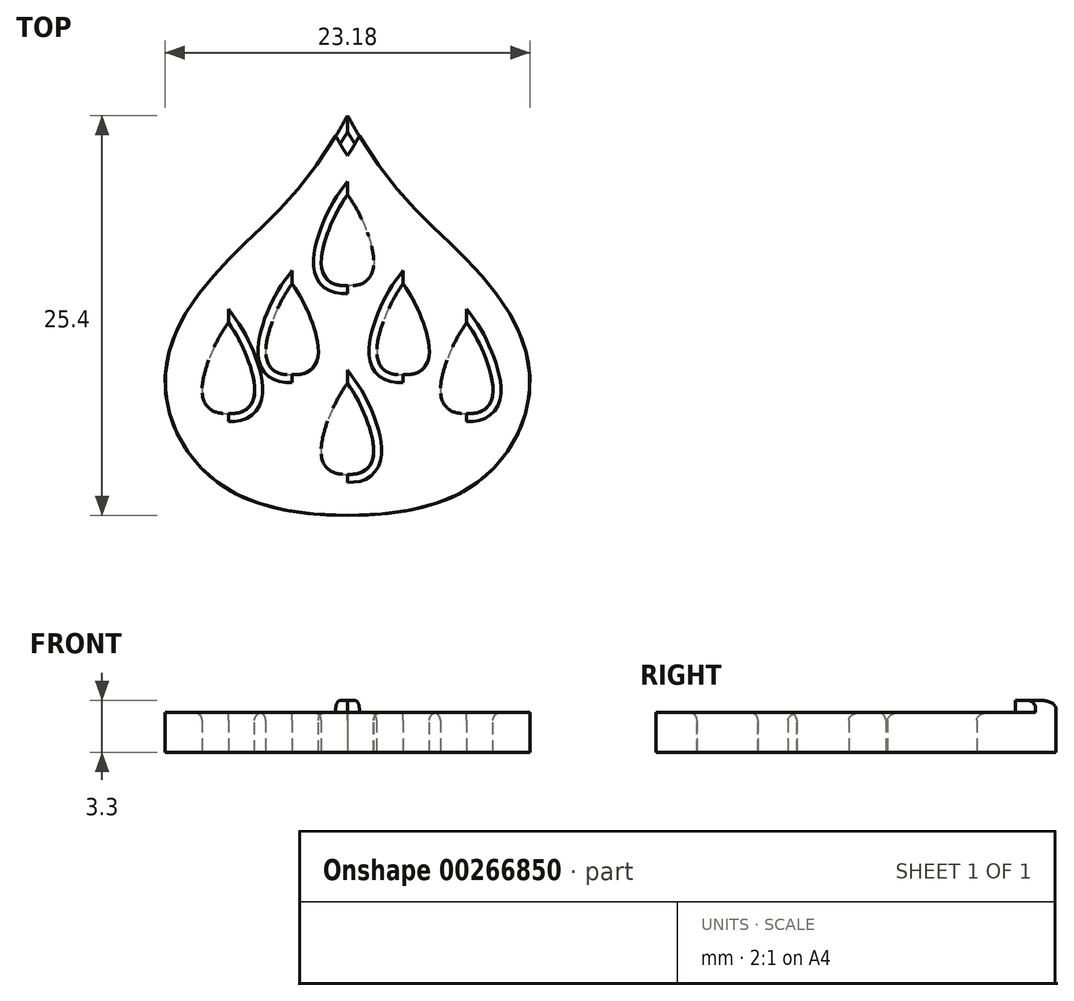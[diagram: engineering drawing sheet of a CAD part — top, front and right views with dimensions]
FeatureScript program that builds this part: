
annotation { "Feature Type Name" : "Feature", "Feature Type Description" : "" }
export const myFeature = defineFeature(function(context is Context, id is Id, definition is map)
    precondition{}
    {
        {
            var Q0;
            Q0=qCreatedBy(makeId("Top.planeOp"),FACE);
            var sketch = newSketch(context, id + "F0", { "sketchPlane" : qUnion([Q0])});
            skLineSegment(sketch, "E0.bottom", {"start": v(12.7, 12.7) * mm, "end": v(-12.7, 12.7) * mm, "construction": true});
            skLineSegment(sketch, "E0.top", {"start": v(12.7, -12.7) * mm, "end": v(-12.7, -12.7) * mm, "construction": true});
            skLineSegment(sketch, "E0.left", {"start": v(12.7, 12.7) * mm, "end": v(12.7, -12.7) * mm, "construction": true});
            skLineSegment(sketch, "E0.right", {"start": v(-12.7, 12.7) * mm, "end": v(-12.7, -12.7) * mm, "construction": true});
            skPoint(sketch, "E0.middle", {"position": v(0, 0) * mm});
            skLineSegment(sketch, "E1", {"start": v(0, 0) * mm, "end": v(0, 12.7) * mm});
            skFitSpline(sketch, "E2", {"points": [v(0, 12.7) * mm, v(-7.85, 3.25) * mm, v(-11.53, -3.23) * mm, v(-9.55, -9.42) * mm, v(0, -12.7) * mm], "startDerivative": vector(-29.48, -53.74) * mm, "endDerivative": vector(54.28, 0) * mm});
            skFitSpline(sketch, "E3.MirrorCS", {"points": [v(0, 12.7) * mm, v(7.85, 3.25) * mm, v(11.53, -3.23) * mm, v(9.55, -9.42) * mm, v(0, -12.7) * mm], "startDerivative": vector(29.48, -53.74) * mm, "endDerivative": vector(-54.28, 0) * mm});
            skSolve(sketch);
        }
        {
            var Q0;
            Q0 = qSketchRegion(id + "F0", true);
            extrude(context, id + "F1", {"entities" : qUnion([Q0]), "depth" : 2.54 * mm});
        }
        {
            var Q0;
            Q0=makeQuery(id+"F1.opExtrude","CAP_FACE",FACE,{"disambiguationData":[OSD([sQuery(id+"F0.wireOp",EDGE,"E2"),sQuery(id+"F0.wireOp",EDGE,"E3.MirrorCS")])],"isStart":false});
            var sketch = newSketch(context, id + "F2", { "sketchPlane" : qUnion([Q0])});
            skFitSpline(sketch, "E4.0", {"points": [v(1.11, 12.09) * mm, v(0.47, 10.91) * mm, v(-0.84, 8.96) * mm, v(-2.8, 6.92) * mm, v(-4.32, 5.7) * mm, v(-5.41, 4.86) * mm, v(-6.04, 4.34) * mm, v(-6.52, 3.92) * mm, v(-6.97, 3.47) * mm, v(-7.52, 2.86) * mm, v(-8.14, 2.04) * mm, v(-8.9, 0.85) * mm, v(-9.67, -0.74) * mm, v(-10.14, -2.37) * mm, v(-10.3, -3.58) * mm, v(-10.31, -4.75) * mm, v(-10.07, -6.12) * mm, v(-9.4, -7.6) * mm, v(-8.4, -8.88) * mm, v(-7.07, -9.94) * mm, v(-5.31, -10.76) * mm, v(-3.02, -11.3) * mm, v(-1.08, -11.43) * mm, v(0, -11.43) * mm]});
            skFitSpline(sketch, "E4.1", {"points": [v(-1.11, 12.09) * mm, v(-0.47, 10.91) * mm, v(0.84, 8.96) * mm, v(2.8, 6.92) * mm, v(4.32, 5.7) * mm, v(5.41, 4.86) * mm, v(6.04, 4.34) * mm, v(6.52, 3.92) * mm, v(6.97, 3.47) * mm, v(7.52, 2.86) * mm, v(8.14, 2.04) * mm, v(8.9, 0.85) * mm, v(9.67, -0.74) * mm, v(10.14, -2.37) * mm, v(10.3, -3.58) * mm, v(10.31, -4.75) * mm, v(10.07, -6.12) * mm, v(9.4, -7.6) * mm, v(8.4, -8.88) * mm, v(7.07, -9.94) * mm, v(5.31, -10.76) * mm, v(3.02, -11.3) * mm, v(1.08, -11.43) * mm, v(0, -11.43) * mm]});
            skFitSpline(sketch, "E5", {"points": [v(-3.29, 3.48) * mm, v(-4.95, 0.86) * mm, v(-5.27, -1.22) * mm, v(-3.29, -2.15) * mm], "startDerivative": vector(-5.74, -16) * mm, "endDerivative": vector(7.25, 0.42) * mm});
            skFitSpline(sketch, "E6.MirrorCS", {"points": [v(-3.29, 3.48) * mm, v(-1.63, 0.86) * mm, v(-1.31, -1.22) * mm, v(-3.29, -2.15) * mm], "startDerivative": vector(5.74, -16) * mm, "endDerivative": vector(-7.25, 0.42) * mm});
            skFitSpline(sketch, "E7", {"points": [v(-7.1, -1.24) * mm, v(-8.76, -3.85) * mm, v(-9.08, -5.94) * mm, v(-7.1, -6.87) * mm], "startDerivative": vector(-5.74, -16) * mm, "endDerivative": vector(7.25, 0.42) * mm});
            skFitSpline(sketch, "E8.MirrorCS", {"points": [v(-7.1, -1.24) * mm, v(-5.44, -3.85) * mm, v(-5.12, -5.94) * mm, v(-7.1, -6.87) * mm], "startDerivative": vector(5.74, -16) * mm, "endDerivative": vector(-7.25, 0.42) * mm});
            skFitSpline(sketch, "E9", {"points": [v(0.05, -4.16) * mm, v(-1.6, -6.77) * mm, v(-1.93, -8.85) * mm, v(0.05, -9.78) * mm], "startDerivative": vector(-5.74, -16) * mm, "endDerivative": vector(7.25, 0.42) * mm});
            skFitSpline(sketch, "E10.MirrorCS", {"points": [v(0.05, -4.16) * mm, v(1.7, -6.77) * mm, v(2.03, -8.85) * mm, v(0.05, -9.78) * mm], "startDerivative": vector(5.74, -16) * mm, "endDerivative": vector(-7.25, 0.42) * mm});
            skFitSpline(sketch, "E11", {"points": [v(0.05, 8.08) * mm, v(-1.6, 5.47) * mm, v(-1.93, 3.39) * mm, v(0.05, 2.46) * mm], "startDerivative": vector(-5.74, -16) * mm, "endDerivative": vector(7.25, 0.42) * mm});
            skFitSpline(sketch, "E12.MirrorCS", {"points": [v(0.05, 8.08) * mm, v(1.7, 5.47) * mm, v(2.03, 3.39) * mm, v(0.05, 2.46) * mm], "startDerivative": vector(5.74, -16) * mm, "endDerivative": vector(-7.25, 0.42) * mm});
            skLineSegment(sketch, "E13", {"start": v(0, 10.2) * mm, "end": v(0, 12.7) * mm});
            skFitSpline(sketch, "E14.MirrorCS", {"points": [v(7.1, -1.24) * mm, v(5.44, -3.85) * mm, v(5.12, -5.94) * mm, v(7.1, -6.87) * mm], "startDerivative": vector(-5.74, -16) * mm, "endDerivative": vector(7.25, 0.42) * mm});
            skFitSpline(sketch, "E15.MirrorCS", {"points": [v(7.1, -1.24) * mm, v(8.76, -3.85) * mm, v(9.08, -5.94) * mm, v(7.1, -6.87) * mm], "startDerivative": vector(5.74, -16) * mm, "endDerivative": vector(-7.25, 0.42) * mm});
            skFitSpline(sketch, "E16.MirrorCS", {"points": [v(3.29, 3.48) * mm, v(4.95, 0.86) * mm, v(5.27, -1.22) * mm, v(3.29, -2.15) * mm], "startDerivative": vector(5.74, -16) * mm, "endDerivative": vector(-7.25, 0.42) * mm});
            skFitSpline(sketch, "E17.MirrorCS", {"points": [v(3.29, 3.48) * mm, v(1.63, 0.86) * mm, v(1.31, -1.22) * mm, v(3.29, -2.15) * mm], "startDerivative": vector(-5.74, -16) * mm, "endDerivative": vector(7.25, 0.42) * mm});
            skSolve(sketch);
        }
        {
            var Q0;
            Q0=makeQuery(id+"F2.imprint","IMPRINT",FACE,{"disambiguationData":[TD([[makeQuery(id+"F2.imprint","IMPRINT",EDGE,{"derivedFrom":sQuery(id+"F2.wireOp",EDGE,"E4.0")}),-1.0]])]});
            extrude(context, id + "F3", {"entities" : qUnion([Q0]), "operationType" : NewBodyOperationType.ADD, "depth" : 0.76 * mm});
        }
        {
            var Q0;
            Q0=qCreatedBy(makeId("Top.planeOp"),FACE);
            var sketch = newSketch(context, id + "F4", { "sketchPlane" : qUnion([Q0])});
            skFitSpline(sketch, "E18", {"points": [v(0, 7.67) * mm, v(-1.66, 3.17) * mm, v(-0.92, 2.03) * mm, v(0, 1.9) * mm], "startDerivative": vector(-5.41, -7.3) * mm, "endDerivative": vector(3.85, 0.13) * mm});
            skLineSegment(sketch, "E19", {"start": v(0, 7.67) * mm, "end": v(0, 1.9) * mm});
            skFitSpline(sketch, "E20.MirrorCS", {"points": [v(0, 7.67) * mm, v(1.66, 3.17) * mm, v(0.92, 2.03) * mm, v(0, 1.9) * mm], "startDerivative": vector(5.41, -7.3) * mm, "endDerivative": vector(-3.85, 0.13) * mm});
            skFitSpline(sketch, "E21", {"points": [v(-0.01, -4.32) * mm, v(-1.67, -8.82) * mm, v(-0.93, -9.95) * mm, v(-0.01, -10.09) * mm], "startDerivative": vector(-5.41, -7.3) * mm, "endDerivative": vector(3.85, 0.13) * mm});
            skFitSpline(sketch, "E22.MirrorCS", {"points": [v(-0.01, -4.32) * mm, v(1.65, -8.82) * mm, v(0.9, -9.95) * mm, v(-0.01, -10.09) * mm], "startDerivative": vector(5.41, -7.3) * mm, "endDerivative": vector(-3.85, 0.13) * mm});
            skFitSpline(sketch, "E23", {"points": [v(-3.53, 2.01) * mm, v(-5.19, -2.5) * mm, v(-4.44, -3.63) * mm, v(-3.53, -3.76) * mm], "startDerivative": vector(-5.41, -7.3) * mm, "endDerivative": vector(3.85, 0.13) * mm});
            skFitSpline(sketch, "E24.MirrorCS", {"points": [v(-3.53, 2.01) * mm, v(-1.86, -2.5) * mm, v(-2.6, -3.63) * mm, v(-3.53, -3.76) * mm], "startDerivative": vector(5.41, -7.3) * mm, "endDerivative": vector(-3.85, 0.13) * mm});
            skFitSpline(sketch, "E25", {"points": [v(-7.57, -0.45) * mm, v(-9.23, -4.95) * mm, v(-8.49, -6.1) * mm, v(-7.57, -6.22) * mm], "startDerivative": vector(-5.41, -7.3) * mm, "endDerivative": vector(3.85, 0.13) * mm});
            skFitSpline(sketch, "E26.MirrorCS", {"points": [v(-7.57, -0.45) * mm, v(-5.9, -4.95) * mm, v(-6.65, -6.1) * mm, v(-7.57, -6.22) * mm], "startDerivative": vector(5.41, -7.3) * mm, "endDerivative": vector(-3.85, 0.13) * mm});
            skFitSpline(sketch, "E27.MirrorCS", {"points": [v(3.53, 2.01) * mm, v(1.86, -2.5) * mm, v(2.6, -3.63) * mm, v(3.53, -3.76) * mm], "startDerivative": vector(-5.41, -7.3) * mm, "endDerivative": vector(3.85, 0.13) * mm});
            skFitSpline(sketch, "E28.MirrorCS", {"points": [v(3.53, 2.01) * mm, v(5.19, -2.5) * mm, v(4.44, -3.63) * mm, v(3.53, -3.76) * mm], "startDerivative": vector(5.41, -7.3) * mm, "endDerivative": vector(-3.85, 0.13) * mm});
            skFitSpline(sketch, "E29.MirrorCS", {"points": [v(7.57, -0.45) * mm, v(5.9, -4.95) * mm, v(6.65, -6.1) * mm, v(7.57, -6.22) * mm], "startDerivative": vector(-5.41, -7.3) * mm, "endDerivative": vector(3.85, 0.13) * mm});
            skFitSpline(sketch, "E30.MirrorCS", {"points": [v(7.57, -0.45) * mm, v(9.23, -4.95) * mm, v(8.49, -6.1) * mm, v(7.57, -6.22) * mm], "startDerivative": vector(5.41, -7.3) * mm, "endDerivative": vector(-3.85, 0.13) * mm});
            skSolve(sketch);
        }
        {
            var Q0;
            Q0 = qSketchRegion(id + "F4", true);
            extrude(context, id + "F5", {"entities" : qUnion([Q0]), "operationType" : NewBodyOperationType.REMOVE, "depth" : 25.4 * mm});
        }
        {
            var Q0;
            Q0=makeQuery(id+"F3.opExtrude","CAP_EDGE",EDGE,{"disambiguationData":[OSD([sQuery(id+"F0.wireOp",EDGE,"E2")])],"isStart":false});
            var Q1;
            Q1=makeQuery(id+"F3.opExtrude","CAP_EDGE",EDGE,{"disambiguationData":[OSD([sQuery(id+"F0.wireOp",EDGE,"E3.MirrorCS")])],"isStart":false});
            var Q2;
            Q2=makeQuery(id+"F5.boolean.opBoolean","INTERSECT",EDGE,{"derivedFrom":[makeQuery(id+"F1.opExtrude","CAP_FACE",FACE,{"disambiguationData":[OSD([sQuery(id+"F0.wireOp",EDGE,"E2"),sQuery(id+"F0.wireOp",EDGE,"E3.MirrorCS")])],"isStart":false}),makeQuery(id+"F5.opExtrude","SWEPT_FACE",FACE,{"disambiguationData":[OSD([sQuery(id+"F4.wireOp",EDGE,"E23")])]})]});
            var Q3;
            Q3=makeQuery(id+"F5.boolean.opBoolean","INTERSECT",EDGE,{"derivedFrom":[makeQuery(id+"F1.opExtrude","CAP_FACE",FACE,{"disambiguationData":[OSD([sQuery(id+"F0.wireOp",EDGE,"E2"),sQuery(id+"F0.wireOp",EDGE,"E3.MirrorCS")])],"isStart":false}),makeQuery(id+"F5.opExtrude","SWEPT_FACE",FACE,{"disambiguationData":[OSD([sQuery(id+"F4.wireOp",EDGE,"E24.MirrorCS")])]})]});
            var Q4;
            Q4=makeQuery(id+"F5.boolean.opBoolean","INTERSECT",EDGE,{"derivedFrom":[makeQuery(id+"F1.opExtrude","CAP_FACE",FACE,{"disambiguationData":[OSD([sQuery(id+"F0.wireOp",EDGE,"E2"),sQuery(id+"F0.wireOp",EDGE,"E3.MirrorCS")])],"isStart":false}),makeQuery(id+"F5.opExtrude","SWEPT_FACE",FACE,{"disambiguationData":[OSD([sQuery(id+"F4.wireOp",EDGE,"E18")])]})]});
            var Q5;
            Q5=makeQuery(id+"F5.boolean.opBoolean","INTERSECT",EDGE,{"derivedFrom":[makeQuery(id+"F1.opExtrude","CAP_FACE",FACE,{"disambiguationData":[OSD([sQuery(id+"F0.wireOp",EDGE,"E2"),sQuery(id+"F0.wireOp",EDGE,"E3.MirrorCS")])],"isStart":false}),makeQuery(id+"F5.opExtrude","SWEPT_FACE",FACE,{"disambiguationData":[OSD([sQuery(id+"F4.wireOp",EDGE,"E20.MirrorCS")])]})]});
            var Q6;
            Q6=makeQuery(id+"F5.boolean.opBoolean","INTERSECT",EDGE,{"derivedFrom":[makeQuery(id+"F1.opExtrude","CAP_FACE",FACE,{"disambiguationData":[OSD([sQuery(id+"F0.wireOp",EDGE,"E2"),sQuery(id+"F0.wireOp",EDGE,"E3.MirrorCS")])],"isStart":false}),makeQuery(id+"F5.opExtrude","SWEPT_FACE",FACE,{"disambiguationData":[OSD([sQuery(id+"F4.wireOp",EDGE,"E27.MirrorCS")])]})]});
            var Q7;
            Q7=makeQuery(id+"F5.boolean.opBoolean","INTERSECT",EDGE,{"derivedFrom":[makeQuery(id+"F1.opExtrude","CAP_FACE",FACE,{"disambiguationData":[OSD([sQuery(id+"F0.wireOp",EDGE,"E2"),sQuery(id+"F0.wireOp",EDGE,"E3.MirrorCS")])],"isStart":false}),makeQuery(id+"F5.opExtrude","SWEPT_FACE",FACE,{"disambiguationData":[OSD([sQuery(id+"F4.wireOp",EDGE,"E28.MirrorCS")])]})]});
            var Q8;
            Q8=makeQuery(id+"F5.boolean.opBoolean","INTERSECT",EDGE,{"derivedFrom":[makeQuery(id+"F1.opExtrude","CAP_FACE",FACE,{"disambiguationData":[OSD([sQuery(id+"F0.wireOp",EDGE,"E2"),sQuery(id+"F0.wireOp",EDGE,"E3.MirrorCS")])],"isStart":false}),makeQuery(id+"F5.opExtrude","SWEPT_FACE",FACE,{"disambiguationData":[OSD([sQuery(id+"F4.wireOp",EDGE,"E30.MirrorCS")])]})]});
            var Q9;
            Q9=makeQuery(id+"F5.boolean.opBoolean","INTERSECT",EDGE,{"derivedFrom":[makeQuery(id+"F1.opExtrude","CAP_FACE",FACE,{"disambiguationData":[OSD([sQuery(id+"F0.wireOp",EDGE,"E2"),sQuery(id+"F0.wireOp",EDGE,"E3.MirrorCS")])],"isStart":false}),makeQuery(id+"F5.opExtrude","SWEPT_FACE",FACE,{"disambiguationData":[OSD([sQuery(id+"F4.wireOp",EDGE,"E29.MirrorCS")])]})]});
            var Q10;
            Q10=makeQuery(id+"F5.boolean.opBoolean","INTERSECT",EDGE,{"derivedFrom":[makeQuery(id+"F1.opExtrude","CAP_FACE",FACE,{"disambiguationData":[OSD([sQuery(id+"F0.wireOp",EDGE,"E2"),sQuery(id+"F0.wireOp",EDGE,"E3.MirrorCS")])],"isStart":false}),makeQuery(id+"F5.opExtrude","SWEPT_FACE",FACE,{"disambiguationData":[OSD([sQuery(id+"F4.wireOp",EDGE,"E22.MirrorCS")])]})]});
            var Q11;
            Q11=makeQuery(id+"F5.boolean.opBoolean","INTERSECT",EDGE,{"derivedFrom":[makeQuery(id+"F1.opExtrude","CAP_FACE",FACE,{"disambiguationData":[OSD([sQuery(id+"F0.wireOp",EDGE,"E2"),sQuery(id+"F0.wireOp",EDGE,"E3.MirrorCS")])],"isStart":false}),makeQuery(id+"F5.opExtrude","SWEPT_FACE",FACE,{"disambiguationData":[OSD([sQuery(id+"F4.wireOp",EDGE,"E21")])]})]});
            var Q12;
            Q12=makeQuery(id+"F5.boolean.opBoolean","INTERSECT",EDGE,{"derivedFrom":[makeQuery(id+"F1.opExtrude","CAP_FACE",FACE,{"disambiguationData":[OSD([sQuery(id+"F0.wireOp",EDGE,"E2"),sQuery(id+"F0.wireOp",EDGE,"E3.MirrorCS")])],"isStart":false}),makeQuery(id+"F5.opExtrude","SWEPT_FACE",FACE,{"disambiguationData":[OSD([sQuery(id+"F4.wireOp",EDGE,"E26.MirrorCS")])]})]});
            var Q13;
            Q13=makeQuery(id+"F5.boolean.opBoolean","INTERSECT",EDGE,{"derivedFrom":[makeQuery(id+"F1.opExtrude","CAP_FACE",FACE,{"disambiguationData":[OSD([sQuery(id+"F0.wireOp",EDGE,"E2"),sQuery(id+"F0.wireOp",EDGE,"E3.MirrorCS")])],"isStart":false}),makeQuery(id+"F5.opExtrude","SWEPT_FACE",FACE,{"disambiguationData":[OSD([sQuery(id+"F4.wireOp",EDGE,"E25")])]})]});
            fillet(context, id + "F6", {"entities" : qUnion([Q0, Q1, Q2, Q3, Q4, Q5, Q6, Q7, Q8, Q9, Q10, Q11, Q12, Q13]), "radius" : 0.5 * mm, "tangentPropagation" : true, "allowEdgeOverflow" : false});
        }
    });
